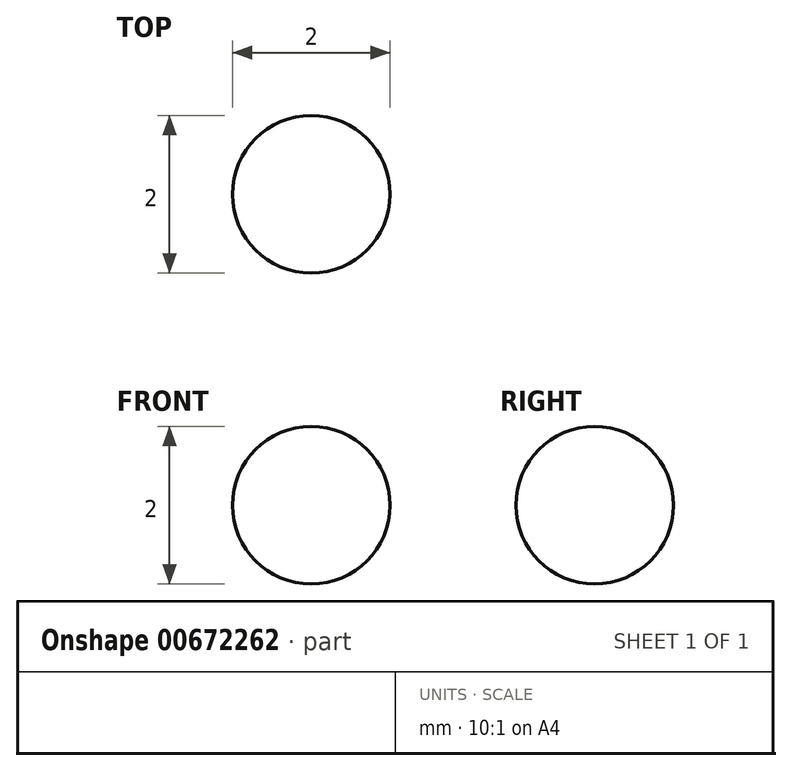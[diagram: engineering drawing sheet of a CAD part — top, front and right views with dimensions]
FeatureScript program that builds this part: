
annotation { "Feature Type Name" : "Feature", "Feature Type Description" : "" }
export const myFeature = defineFeature(function(context is Context, id is Id, definition is map)
    precondition{}
    {
        {
            var Q0;
            Q0=qCreatedBy(makeId("Top.planeOp"),FACE);
            var sketch = newSketch(context, id + "F0", { "sketchPlane" : qUnion([Q0])});
            skArc(sketch, "E0", {"start": v(0, -1) * mm, "mid": v(1, 0) * mm, "end": v(0, 1) * mm});
            skLineSegment(sketch, "E1", {"start": v(0, 1) * mm, "end": v(0, -1) * mm});
            skLineSegment(sketch, "E2", {"start": v(0, 1.67) * mm, "end": v(0, -1.8) * mm, "construction": true});
            skSolve(sketch);
        }
        {
            var Q0;
            Q0 = qSketchRegion(id + "F0", true);
            var Q1;
            Q1=sQuery(id+"F0.wireOp",EDGE,"E2");
            revolve(context, id + "F1", {"entities" : qUnion([Q0]), "axis" : qUnion([Q1]), "revolveType" : RevolveType.FULL});
        }
    });
